# Revit family: Maxlogic Detectors
name_source: partatom
category: Fire Alarm Devices
units: mm (PartAtom-declared; Revit-internal decimal feet)

## family parameters
Cut with Voids When Loaded = No
Host = Face
Maintain Annotation Orientation = Yes
OmniClass Number = 23.85.30.21
OmniClass Title = Environmental Detection/Registration
Part Type = Normal
Room Calculation Point = No
Round Connector Dimension = Use Diameter
Shared = No

## types (10) — shared parameters
Color = White
Compatible sockets = ML-0140
Compatible sockets 2 = ML-0141
Fax Number = (+)90 216 466 45 10
Installation Manual = https://mavilielektronik.com
Main Material = White Plastic PC/ABS
Manufacturer = Mavili Elektronik Ticaret A.Ş.
Model = Maxlogic
Nominal Depth = 51 mm
Nominal Height = 106 mm
Nominal Width = 106 mm
Operating temperature = (-10°C) - (+50°C)
Operatonal Voltage (default) = 26 V/DC
Recessed mounting base = ML-0150
Secondary Material = Plastic
URL = https://www.mavili.com.tr
Warranty Duration Labor = 2
Warranty Duration Parts = 2
Warranty Duration Unit = Year
Weatherproof surface mounting back box = ML-0121
zero-valued in all types: Cost, Default Elevation

## per-type parameters (varying)
| type | Code Performance | Description | Detectıon radıus | Device Adress Setup | Heat Circle | Indicator output | Mounting surface | Multisensor Circle | Operating voltage range | Product Code | Public Works Pose Number | Weight |
| Maxlogic Conventional Optical smoke dedector | EN 54-7 | Conventional Optical smoke dedector | 6,2 m |  | No | MG-4000 | Ceiling mount | No | 10-30V/DC | ML-2110 | 832-106 | 140 gr |
| Maxlogic Intelligent Addressable Photo-Electric Smoke Detector | EN 54-7 | Intelligent Addressable Photo-Electric Smoke Detector | 6,2 m | The address is given to devices by addressable programmer | No | MG-4000.A | Ceiling mount | No | 18-33V/DC | ML-1110 | 833-500 | 100 gr |
| Maxlogic Intelligent Addressable Photo-Electric Smoke Detector, Short Circuit Isolator | EN 54-7 / EN 54-17 | Intelligent Addressable Photo-Electric Smoke Detector, Short Circuit Isolator | 6,2 m | The address is given to devices by addressable programmer | No | MG-4000.A | Ceiling mount | No | 18-33V/DC | ML-1110.SCI | 833-501 | 100 gr |
| Maxlogic Conventional Fixed heat detector | EN 54-5 | Conventional Fixed heat detector | 4,5 m |  | Yes | MG-4000 | Ceiling mount | No | 10-30V/DC | ML-2120 | 832-102 | 135 gr |
| Maxlogic Conventional Rate of rise heat detector | EN 54-5 | Conventional Rate of rise heat detector | 4,5 m |  | Yes | MG-4000 | ceiling mount | No | 10-30V/DC | ML-2130 | 832-103 | 135 gr |
| Maxlogic Intelligent Addressable Heat Detector | EN 54-5 | Intelligent Addressable Heat Detector | 4,5 m | The address is given to devices by addressable programmer | Yes | MG-4000.A | Ceiling mount | No | 18-33V/DC | ML-1130 | 833-520 | 95 gr |
| Maxlogic Intelligent Addressable Heat Detector, Short Circuit Isolator | EN 54-5 / EN 54-17 | Intelligent Addressable Heat Detector, Short Circuit Isolator | 4,5 m | The address is given to devices by addressable programmer | Yes | MG-4000.A | Ceiling mount | No | 18-33V/DC | ML-1130.SCI | 833-521 | 95 gr |
| Maxlogic Conventional Multi-Sensor detector | EN 54-5 / EN 54-7 | Conventional Multi-Sensor detector | 4,5 m |  | Yes | MG-4000 | Ceiling mount | Yes | 10-30V/DC | ML-2140 | 832-109 | 141 gr |
| Maxlogic Intelligent Addressable Multisensor Detector (Photo-Electric Smoke+Heat ) | EN 54-5 / EN 54-7 / EN 54-17 | Intelligent Addressable Multisensor Detector (Photo-Electric Smoke+Heat ) | 4,5 m | The address is given to devices by addressable programmer | Yes | MG-4000.A | Ceiling mount | Yes | 18-33V/DC | ML-1140 | 833-530 | 100 gr |
| Maxlogic Intelligent Addressable Multisensor Detector (Photo-Electric Smoke+Heat ), Short Circuit Isolator | EN 54-5 / EN 54-7 / EN 54-17 | Intelligent Addressable Multisensor Detector (Photo-Electric Smoke+Heat ), Short Circuit Isolator | 4,5 m | The address is given to devices by addressable programmer | Yes | MG-4000.A | Ceiling mount | Yes | 18-33V/DC | ML-1140.SCI | 833-531 | 100 gr |

## geometry (parser evidence)
native form markers: Sweep x1
no freeform markers — native parametric forms only
